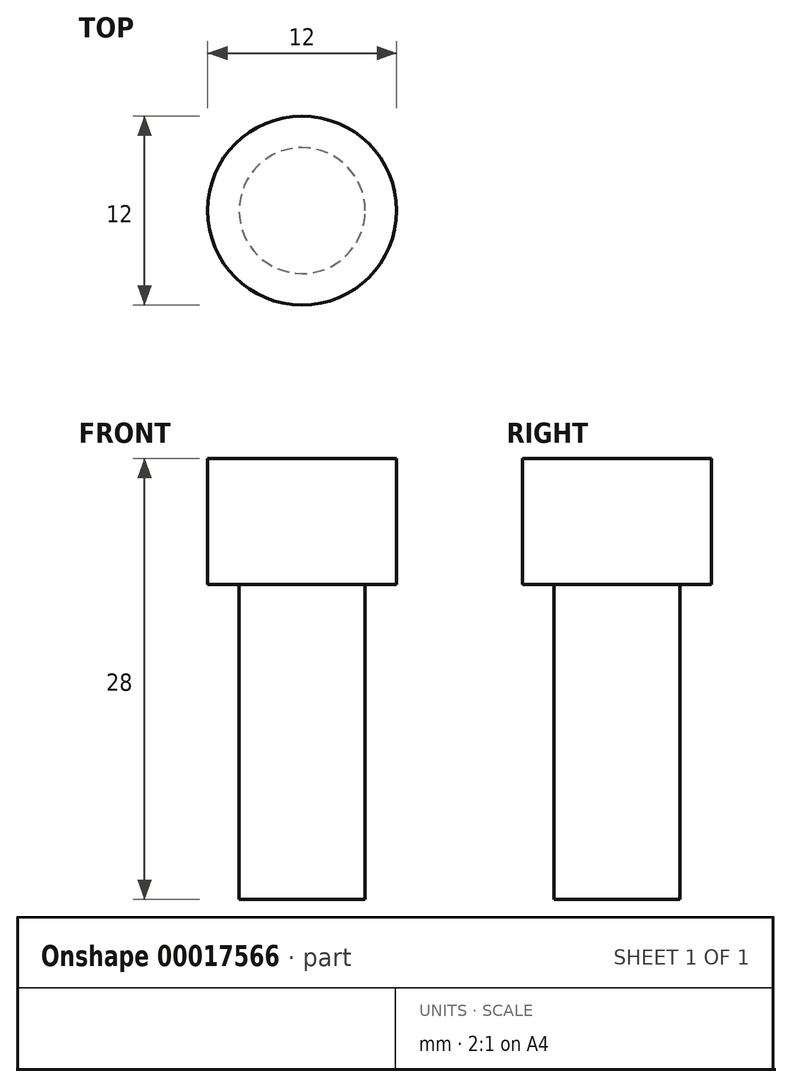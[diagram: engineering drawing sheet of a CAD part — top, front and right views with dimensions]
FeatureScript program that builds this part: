
annotation { "Feature Type Name" : "Feature", "Feature Type Description" : "" }
export const myFeature = defineFeature(function(context is Context, id is Id, definition is map)
    precondition{}
    {
        {
            var Q0;
            Q0=qCreatedBy(makeId("Top.planeOp"),FACE);
            var sketch = newSketch(context, id + "F0", { "sketchPlane" : qUnion([Q0])});
            skCircle(sketch, "E0", {"center": v(0, 0) * mm, "radius": 4 * mm});
            skSolve(sketch);
        }
        {
            var Q0;
            Q0=qSketchRegion(id+"F0",true);
            extrude(context, id + "F1", {"entities" : qUnion([Q0]), "depth" : 20 * mm});
        }
        {
            var Q0;
            Q0=makeQuery(id+"F1.opExtrude","CAP_FACE",FACE,{"disambiguationData":[OSD([sQuery(id+"F0.wireOp",EDGE,"E0")])],"isStart":false});
            var sketch = newSketch(context, id + "F2", { "sketchPlane" : qUnion([Q0])});
            skCircle(sketch, "E1", {"center": v(0, 0) * mm, "radius": 6 * mm});
            skSolve(sketch);
        }
        {
            var Q0;
            Q0=qSketchRegion(id+"F2",true);
            extrude(context, id + "F3", {"entities" : qUnion([Q0]), "operationType" : NewBodyOperationType.ADD, "depth" : 8 * mm});
        }
    });
